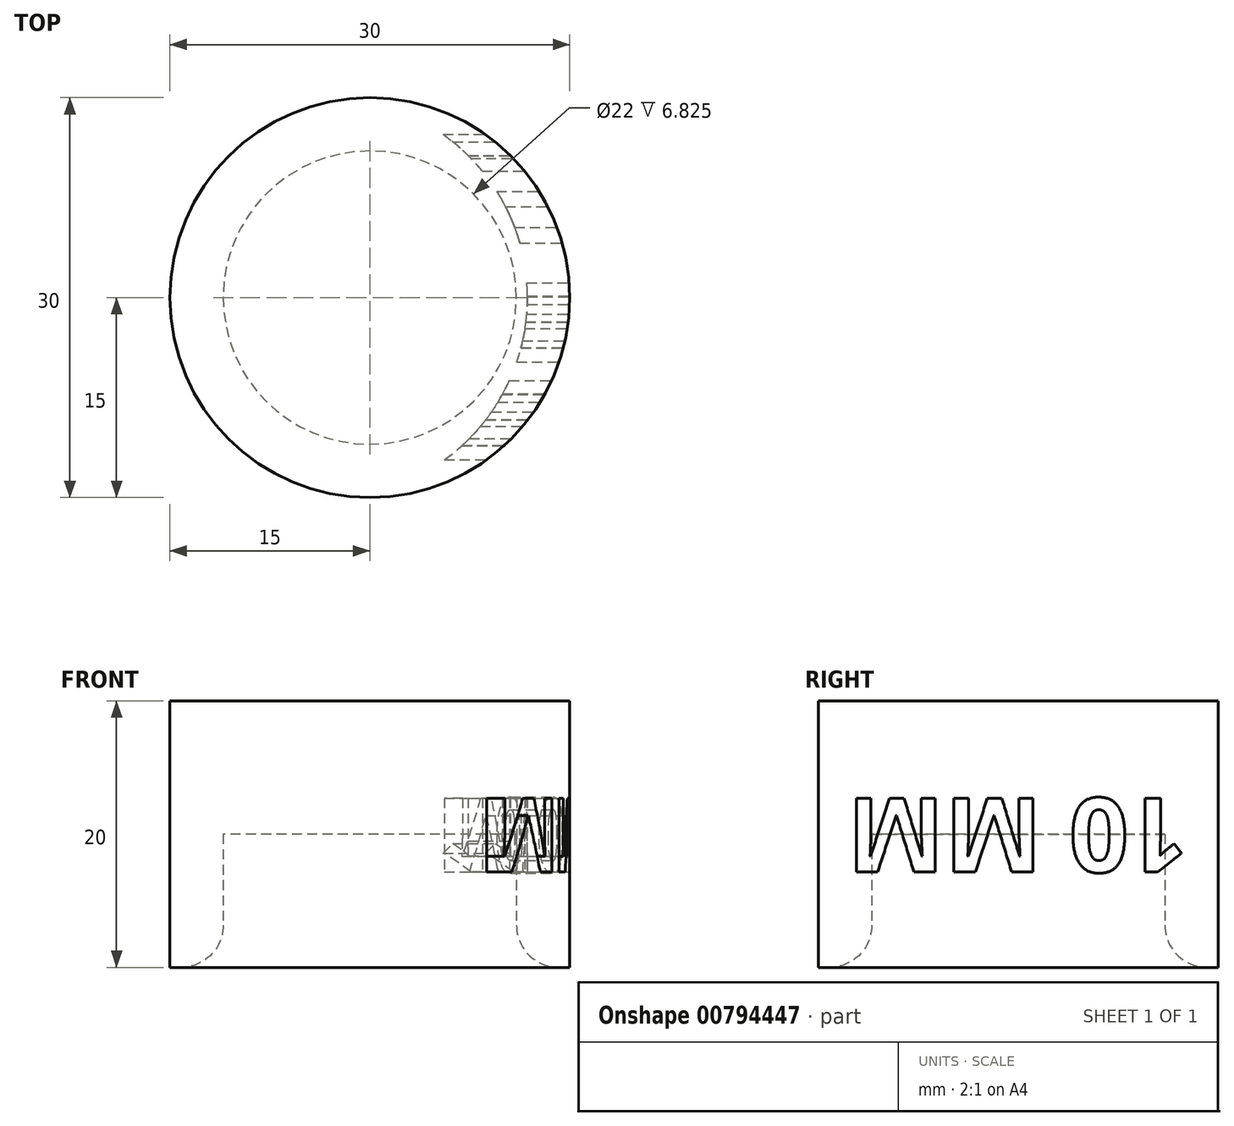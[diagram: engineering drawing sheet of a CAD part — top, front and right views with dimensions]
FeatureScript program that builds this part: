
annotation { "Feature Type Name" : "Feature", "Feature Type Description" : "" }
export const myFeature = defineFeature(function(context is Context, id is Id, definition is map)
    precondition{}
    {
        {
            var Q0;
            Q0=qCreatedBy(makeId("Top.planeOp"),FACE);
            var sketch = newSketch(context, id + "F0", { "sketchPlane" : qUnion([Q0])});
            skCircle(sketch, "E0", {"center": v(0, 0) * mm, "radius": 11 * mm});
            skCircle(sketch, "E1", {"center": v(0, 0) * mm, "radius": 15 * mm});
            skSolve(sketch);
        }
        {
            var Q0;
            Q0=makeQuery(id+"F0.imprint","IMPRINT",FACE,{"disambiguationData":[TD([[makeQuery(id+"F0.imprint","IMPRINT",EDGE,{"derivedFrom":sQuery(id+"F0.wireOp",EDGE,"E0")}),-1.0]])]});
            extrude(context, id + "F1", {"entities" : qUnion([Q0]), "depth" : 10 * mm, "offsetDistance" : 25.4 * mm});
        }
        {
            var Q0;
            Q0=makeQuery(id+"F1.opExtrude","CAP_FACE",FACE,{"disambiguationData":[OSD([sQuery(id+"F0.wireOp",EDGE,"E0"),sQuery(id+"F0.wireOp",EDGE,"E1")])],"isStart":false});
            var sketch = newSketch(context, id + "F2", { "sketchPlane" : qUnion([Q0])});
            skCircle(sketch, "E2.0", {"center": v(0, 0) * mm, "radius": 15 * mm});
            skSolve(sketch);
        }
        {
            var Q0;
            Q0=makeQuery(id+"F2.imprint","IMPRINT",FACE,{"disambiguationData":[TD([[makeQuery(id+"F2.imprint","IMPRINT",EDGE,{"derivedFrom":sQuery(id+"F2.wireOp",EDGE,"E2.0")}),1.0]])]});
            var Q1;
            Q1=makeQuery(id+"F2.imprint","IMPRINT",FACE,{"disambiguationData":[TD([[makeQuery(id+"F2.imprint","IMPRINT",EDGE,{"derivedFrom":makeQuery(id+"F1.opExtrude","CAP_EDGE",EDGE,{"disambiguationData":[OSD([sQuery(id+"F0.wireOp",EDGE,"E0")])],"isStart":false})}),1.0]])]});
            extrude(context, id + "F3", {"entities" : qUnion([Q0, Q1]), "operationType" : NewBodyOperationType.ADD, "depth" : 10 * mm, "offsetDistance" : 25.4 * mm});
        }
        {
            var Q0;
            Q0=makeQuery(id+"F1.opExtrude","CAP_EDGE",EDGE,{"disambiguationData":[OSD([sQuery(id+"F0.wireOp",EDGE,"E0")])],"isStart":true});
            fillet(context, id + "F4", {"entities" : qUnion([Q0]), "radius" : 3.17 * mm, "tangentPropagation" : true, "allowEdgeOverflow" : false});
        }
        {
            var Q0;
            Q0=qCreatedBy(makeId("Right.planeOp"),FACE);
            cPlane(context, id + "F5", {"entities" : qUnion([Q0]), "cplaneType" : CPlaneType.OFFSET, "offset" : 15 * mm, "width" : 152.4 * mm, "height" : 152.4 * mm});
        }
        {
            var Q0;
            Q0=qCreatedBy(id+"F5.planeOp",FACE);
            var sketch = newSketch(context, id + "F6", { "sketchPlane" : qUnion([Q0])});
            skText(sketch, "E3", { "text": "10 MM", "fontName": "OpenSans-Bold.ttf"});
            const initialGuessF6  = {"E3": [0.0127, 0.0127, -1, 0, 0.0056]};
            skSetInitialGuess(sketch, initialGuessF6);
            skSolve(sketch);
        }
        {
            var Q0;
            Q0 = qSketchRegion(id + "F6", true);
            var Q1;
            Q1=makeQuery(id+"F3.boolean.opBoolean","MERGE",FACE,{"derivedFrom":[makeQuery(id+"F1.opExtrude","SWEPT_FACE",FACE,{"disambiguationData":[OSD([sQuery(id+"F0.wireOp",EDGE,"E1")])]}),makeQuery(id+"F3.opExtrude","SWEPT_FACE",FACE,{"disambiguationData":[OSD([sQuery(id+"F2.wireOp",EDGE,"E2.0")])]})]});
            extrude(context, id + "F7", {"entities" : qUnion([Q0]), "operationType" : NewBodyOperationType.REMOVE, "endBound" : BoundingType.UP_TO_SURFACE, "oppositeDirection" : true, "depth" : 25.4 * mm, "endBoundEntityFace" : qUnion([Q1]), "hasOffset" : true, "offsetDistance" : -3.17 * mm});
        }
    });
